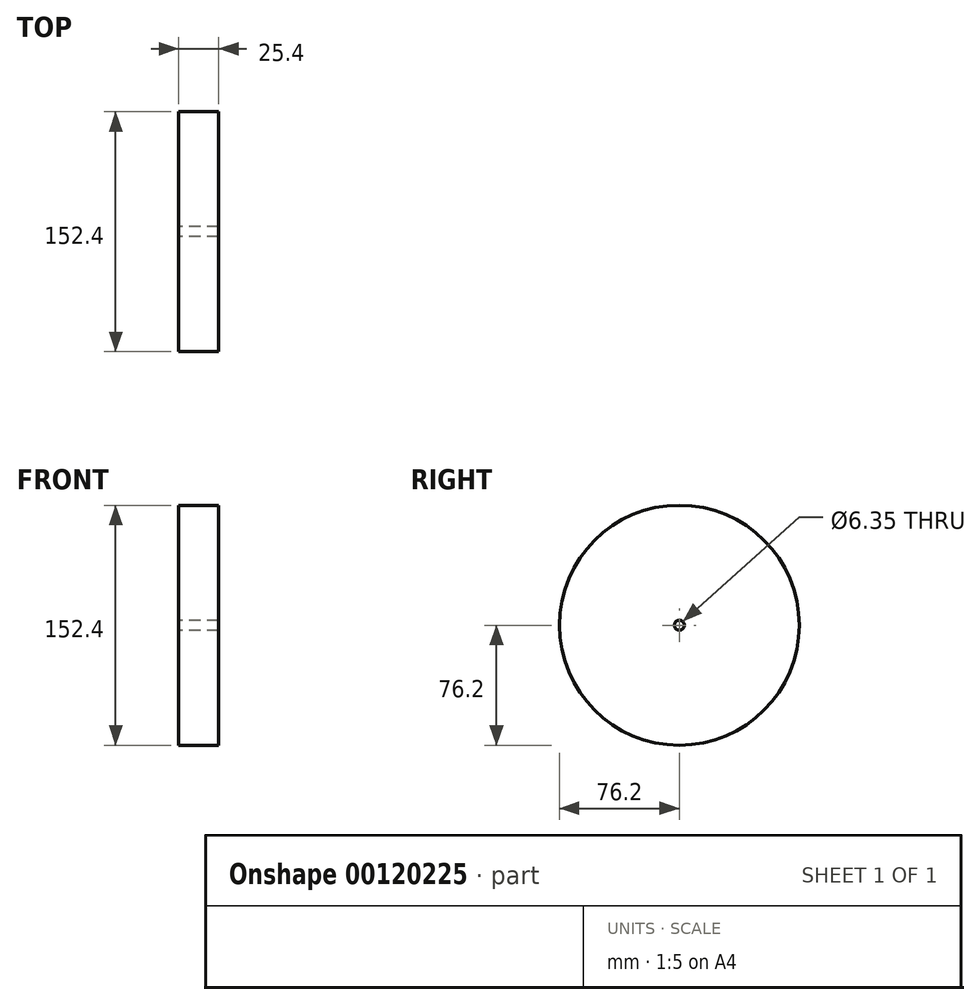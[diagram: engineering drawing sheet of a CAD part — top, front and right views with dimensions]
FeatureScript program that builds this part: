
annotation { "Feature Type Name" : "Feature", "Feature Type Description" : "" }
export const myFeature = defineFeature(function(context is Context, id is Id, definition is map)
    precondition{}
    {
        {
            var Q0;
            Q0=qCreatedBy(makeId("Front.planeOp"),FACE);
            var sketch = newSketch(context, id + "F0", { "sketchPlane" : qUnion([Q0])});
            skLineSegment(sketch, "E0", {"start": v(-139.12, 0) * mm, "end": v(135.16, 0) * mm, "construction": true});
            skLineSegment(sketch, "E1", {"start": v(0, 3.18) * mm, "end": v(0, 76.2) * mm});
            skLineSegment(sketch, "E2", {"start": v(0, 76.2) * mm, "end": v(25.4, 76.2) * mm});
            skLineSegment(sketch, "E3", {"start": v(25.4, 76.2) * mm, "end": v(25.4, 3.18) * mm});
            skLineSegment(sketch, "E4", {"start": v(25.4, 3.18) * mm, "end": v(0, 3.18) * mm});
            skSolve(sketch);
        }
        {
            var Q0;
            Q0 = qSketchRegion(id + "F0", true);
            var Q1;
            Q1=sQuery(id+"F0.wireOp",EDGE,"E0");
            revolve(context, id + "F1", {"entities" : qUnion([Q0]), "axis" : qUnion([Q1]), "revolveType" : RevolveType.FULL});
        }
        {
            var Q0;
            Q0=makeQuery(id+"F1.opRevolve","SWEPT_FACE",FACE,{"disambiguationData":[OSD([sQuery(id+"F0.wireOp",EDGE,"E3")])]});
            var sketch = newSketch(context, id + "F2", { "sketchPlane" : qUnion([Q0])});
            skCircle(sketch, "E5", {"center": v(0, 0) * mm, "radius": 63.5 * mm, "construction": true});
            skSolve(sketch);
        }
    });
